# Revit family: Plumbing_Drainage_Dallmer_CeraFloor-Individual
name_source: partatom
category: Plumbing Fixtures
revit_build: Autodesk Revit 2015 (Build: 20140905_0730(x64)
units: mm (PartAtom-declared; Revit-internal decimal feet)

## types (1)
- CeraFloor Individual
    Assembly Code = D2030300
    BIMobject category = Drainage
    BIMobject category code = plumbing-drainage
    BIMobject main category = Plumbing
    BIMobject main category code = Plumbing
    Brand url = http://www.dallmer.com
    Connector Concentric = Connection : Concentric
    Connector Left = Connection : Left
    Connector Right = Connection : Right
    Description = Shower Channel
    Design country = Germany
    Edition number = 1
    Installation instructions = https://www.dallmer.de
    Keynote = 15150.A2
    Manufacturer = Dallmer
    Manufacturer country = Germany
    Manufacturer name = Dallmer
    Material main = Stainless steel
    Material secondary = Polypropylene
    Model = CeraFloor Individual
    Nominal height = 90 mm  [stored 0.295276 ft]
    Nominal width = 14 mm  [stored 0.0459318 ft]
    Product Guid = e8980a5c-9362-4567-b606-bd9c974b931b
    Product SKU = shower-channels-cerafloor-individual-537478537744
    Product data url = https://bimobject.com
    Product family = Shower channel
    Product group = DallFlex
    Product url = https://www.dallmer.de
    QR code = http://bimobject.com
    Shower Underlay 09x09x40 Floor = DallFlex Floor : Plan 900 x 900 mm, DN 40
    Shower Underlay 09x09x50 Floor = DallFlex Floor : 900 x 900 mm, DN 50
    Shower Underlay 09x09x50 Floor sound = DallFlex Floor : Sound Insulating 900 x 900 mm, DN 50
    Shower Underlay 09x12x40 Floor = DallFlex Floor : Plan 900 x 1200 mm, DN 40
    Shower Underlay 09x12x50 Floor = DallFlex Floor : 900 x 1200 mm, DN 50
    Shower Underlay 09x12x50 Floor sound = DallFlex Floor : Sound Insulating 900 x 1200 mm, DN 50
    Shower Underlay 10x10x40 Floor = DallFlex Floor : Plan 1000 x 1000 mm, DN 40
    Shower Underlay 10x10x50 Floor = DallFlex Floor : 1000 x 1000 mm, DN 50
    Shower Underlay 10x10x50 Floor sound = DallFlex Floor : Sound Insulating 1000 x 1000 mm, DN 50
    Shower Underlay 12x12x40 Floor = DallFlex Floor : Plan 1200 x 1200 mm, DN 40
    Shower Underlay 12x12x50 Floor = DallFlex Floor : 1200 x 1200 mm, DN 50
    Shower Underlay 12x12x50 Floor sound = DallFlex Floor : Sound Insulating 1200 x 1200 mm, DN 50
    Technical description = https://www.dallmer.de
    UNSPSC Code = 40141719
    URL = http://www.dallmer.com
    Uniclass 1.4 Code = JR1
    Uniclass 1.4 Description = Drainage
    Uniclass 2.0 Code = PR-62-24
    Uniclass 2.0 Description = Drainage Traps
    Uniclass 2015 Code = Ac_10_40_67
    Uniclass 2015 Name = Plumbing
    Uniformat II Code = D2010
    Uniformat II Description = Plumbing Fixtures
    Void Height = 20 mm  [stored 0.0656168 ft]
    Weight Net (Kg) = 0
    Youtube clip = https://www.dallmer.de

note: [stored X ft] marks values corroborated as IEEE doubles in the binary element streams (Revit-internal decimal feet)

## geometry (parser evidence)
native form markers: Blend x4, Sweep x15
no freeform markers — native parametric forms only
